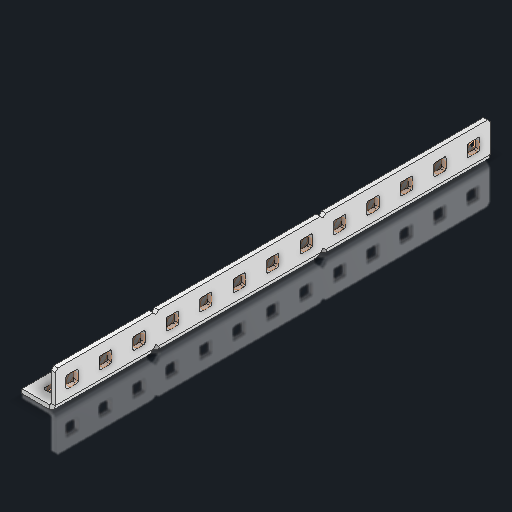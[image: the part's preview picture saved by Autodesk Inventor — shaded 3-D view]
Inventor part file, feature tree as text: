
AUTODESK INVENTOR PART (.ipt)
format: ipt  version: 2023.2 (Build 272271030, 271C)  size: 585,216 bytes
history: native  units: in
note: dims shown in document units (in); Inventor stores cm internally (conversion verified against a paired STEP export)
features: other x58, sketch x8, sheet_metal_op x1
ambient origin geometry x8: Origin, YZ Plane, XZ Plane, XY Plane, X Axis, Y Axis, Z Axis, Center Point
bodies: Solid1 (feature_tree)
feature tree (67):
  other  "Alu C Half 1x3x1x13.ipt"
  other  "Solid1::Alu C Half 1x3x1x13.ipt"
  other  "TaggingFeature1"
  sketch  "Sketch1"  dims[d0=0.3937in]
  sketch  "Sketch2"  dims[d1=0.0625in]
  sketch  "Sketch3"
  sketch  "Sketch7"
  other  "Flange Pattern Sketch"
  sketch  "Sketch8"
  sketch  "Sketch9"
  sheet_metal_op  "Body Pattern Sketch"
  other  "Arc Length"
  sketch  "Sketch13"
  sketch  "Sketch14"
  other  "Flange Pattern Plane"
  other  "Srf1"
  other  "Srf2"
  other  "Srf3"
  other  "Srf4"
  other  "Srf5"
  other  "Srf6"
  other  "Srf7"
  other  "Srf8"
  other  "Srf9"
  other  "Srf10"
  other  "Srf11"
  other  "Srf12"
  other  "Srf13"
  other  "Srf14"
  other  "Srf15"
  other  "Srf16"
  other  "Srf17"
  other  "Srf18"
  other  "Srf19"
  other  "Srf20"
  other  "Srf21"
  other  "Srf22"
  other  "Srf23"
  other  "Srf24"
  other  "Srf25"
  other  "Srf26"
  other  "Srf1::Derived"
  other  "Srf2::Derived"
  other  "Srf1310::Derived"
  other  "Srf1311::Derived"
  other  "Srf1312::Derived"
  other  "Srf1728::Derived"
  other  "Srf1878::Derived"
  other  "Srf1879::Derived"
  other  "Srf1880::Derived"
  other  "Srf1881::Derived"
  other  "Srf1882::Derived"
  other  "Srf1883::Derived"
  other  "Srf1884::Derived"
  other  "Srf91::Derived"
  other  "Srf92::Derived"
  other  "Srf856::Derived"
  other  "Srf1376::Derived"
  other  "Srf1377::Derived"
  other  "Srf1755::Derived"
  other  "Srf1942::Derived"
  other  "Srf1943::Derived"
  other  "Srf1944::Derived"
  other  "Srf1945::Derived"
  other  "Srf1946::Derived"
  other  "Srf1947::Derived"
  other  "Srf1948::Derived"
